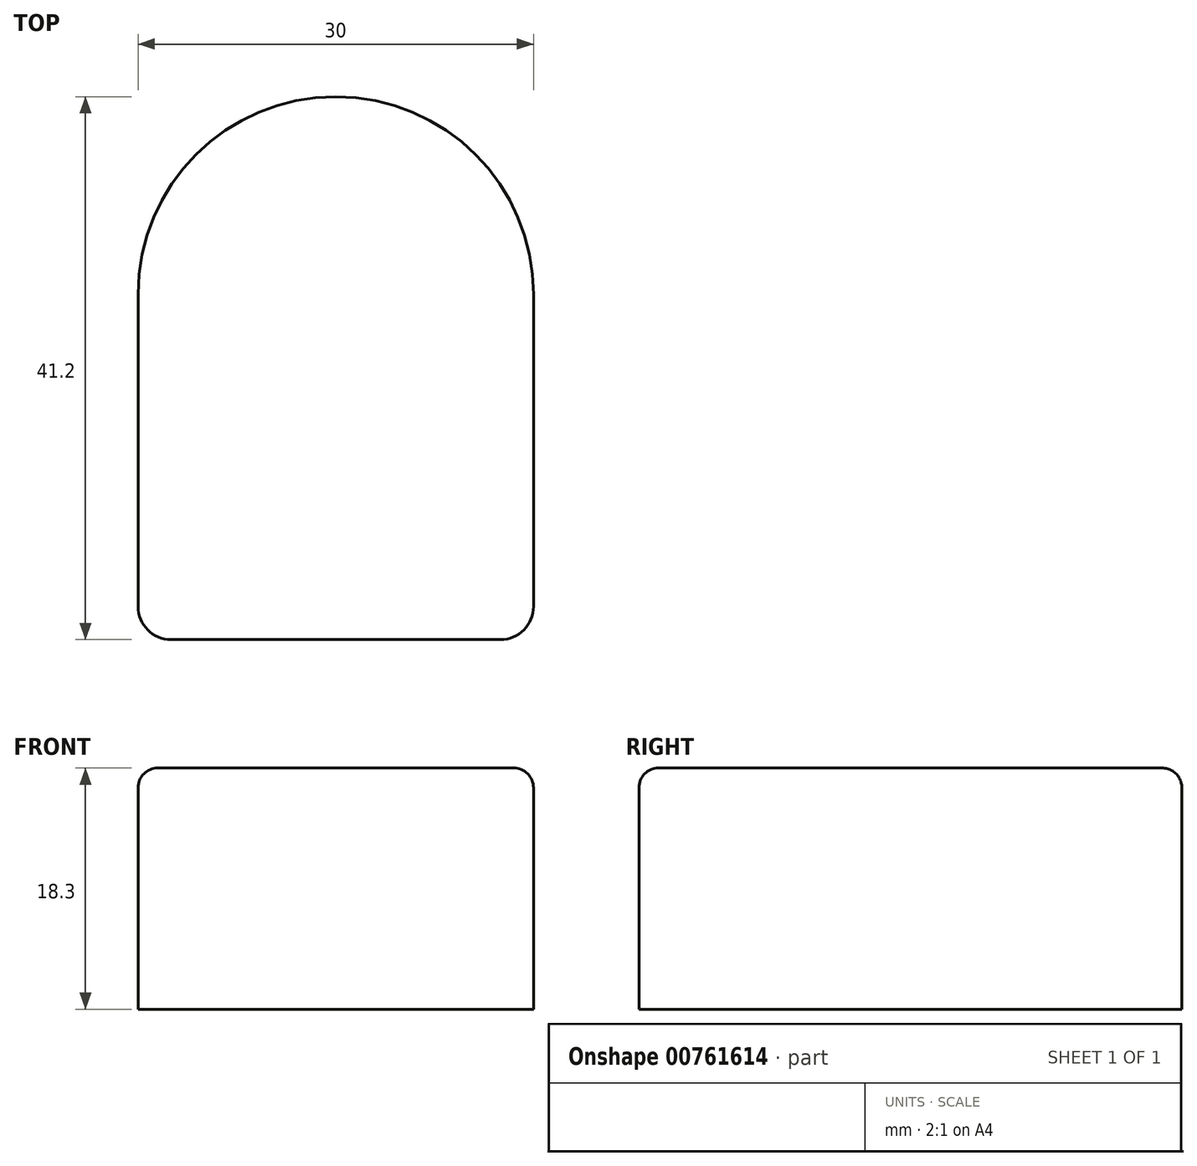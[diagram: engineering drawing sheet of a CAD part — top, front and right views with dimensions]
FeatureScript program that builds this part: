
annotation { "Feature Type Name" : "Feature", "Feature Type Description" : "" }
export const myFeature = defineFeature(function(context is Context, id is Id, definition is map)
    precondition{}
    {
        {
            var Q0;
            Q0=qCreatedBy(makeId("Top.planeOp"),FACE);
            var sketch = newSketch(context, id + "F0", { "sketchPlane" : qUnion([Q0])});
            skLineSegment(sketch, "E0.top", {"start": v(-9.4, 0) * mm, "end": v(15.6, 0) * mm});
            skLineSegment(sketch, "E0.left", {"start": v(-11.9, 26.2) * mm, "end": v(-11.9, 2.5) * mm});
            skLineSegment(sketch, "E0.right", {"start": v(18.1, 26.2) * mm, "end": v(18.1, 2.5) * mm});
            skArc(sketch, "E1", {"start": v(18.1, 26.2) * mm, "mid": v(3.1, 41.2) * mm, "end": v(-11.9, 26.2) * mm});
            skPoint(sketch, "E2.visualSharp", {"position": v(-11.9, 0) * mm});
            skArc(sketch, "E2.filletArc", {"start": v(-11.9, 2.5) * mm, "mid": v(-11.17, 0.73) * mm, "end": v(-9.4, 0) * mm});
            skPoint(sketch, "E3.visualSharp", {"position": v(18.1, 0) * mm});
            skArc(sketch, "E3.filletArc", {"start": v(15.6, 0) * mm, "mid": v(17.37, 0.73) * mm, "end": v(18.1, 2.5) * mm});
            skSolve(sketch);
        }
        {
            var Q0;
            Q0 = qSketchRegion(id + "F0", true);
            extrude(context, id + "F1", {"entities" : qUnion([Q0]), "depth" : 18.3 * mm, "offsetDistance" : 25 * mm});
        }
        {
            var Q0;
            Q0=makeQuery(id+"F1.opExtrude","CAP_FACE",FACE,{"disambiguationData":[OSD([sQuery(id+"F0.wireOp",EDGE,"E0.top"),sQuery(id+"F0.wireOp",EDGE,"E0.left"),sQuery(id+"F0.wireOp",EDGE,"E0.right"),sQuery(id+"F0.wireOp",EDGE,"E1"),sQuery(id+"F0.wireOp",EDGE,"E2.filletArc"),sQuery(id+"F0.wireOp",EDGE,"E3.filletArc")])],"isStart":false});
            fillet(context, id + "F2", {"entities" : qUnion([Q0]), "radius" : 1.5 * mm, "tangentPropagation" : true, "allowEdgeOverflow" : false});
        }
    });
